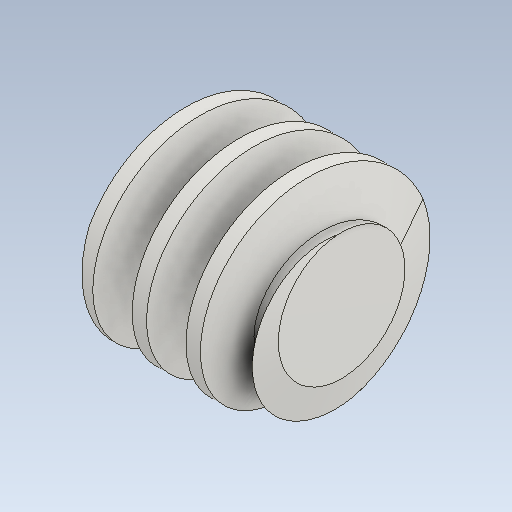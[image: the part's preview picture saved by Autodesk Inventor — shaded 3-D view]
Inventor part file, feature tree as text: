
AUTODESK INVENTOR PART (.ipt)
format: ipt  version: 2021 (Build 250183000, 183)  size: 291,840 bytes
history: native  units: mm (DEFAULTED — no unit token found)
features: other x6, chamfer x2, pattern_circular x2, extrude x1, sketch x1
ambient origin geometry x6: Origin, XZ Plane, X Axis, Y Axis, Z Axis, Center Point
bodies: Solid1 (feature_tree)
feature tree (12):
  extrude  "Base Body"  Depth=10.0mm
  chamfer  "Chamfer1"  Distance=40.0mm
  chamfer  "Chamfer2"  [1 undecoded]
  other  "Tooth Sketch"
  other  "Tooth"
  pattern_circular  "Tooth Pattern"  [2 undecoded]
  other  "Left Tooth"
  pattern_circular  "Left Tooth Pattern"  [2 undecoded]
  other  "Base Body Sketch"
  sketch  "Sketch5"  dims[d4=40.0mm d5=48.0mm d6=40.0mm d7=0.0mm d8=3.348526mm d9=9.2mm d10=3.348526mm d11=9.2mm d12=19.198622mm d14=3.1425mm d24=19.198622mm d25=31.415927mm d26=3.141593mm d27=14.8mm d28=20.0mm d29=24.24mm d30=12.566371mm d31=10.0mm d32=60.0mm d33=0.0mm d34=90.0deg d35=90.0deg d36=0.0mm d37=0.0mm d44=10.0mm d46=360.0deg d47=45.0deg d48=45.0deg d49=40.0168mm d50=0.0mm d54=0.0mm d56=0.0mm d59=40.0mm d60=10.0mm d61=0.0mm d62=12.566371mm d63=10.0mm d64=60.0mm d65=0.0mm d66=90.0deg d67=90.0deg d68=0.0mm d69=0.0mm d70=10.0mm d71=10.0mm d72=10.0mm d73=360.0deg d75=10.0mm d76=10.0mm d77=0.0mm d79=40.0168mm d80=0.0mm]
  other  "Srf1"
  other  "Pitch Diameter"
note: 5 required parameter values undecoded (feature->parameter linkage not recoverable at this tier; creation-order binding heuristic only, values carry confidence <= 0.55)
